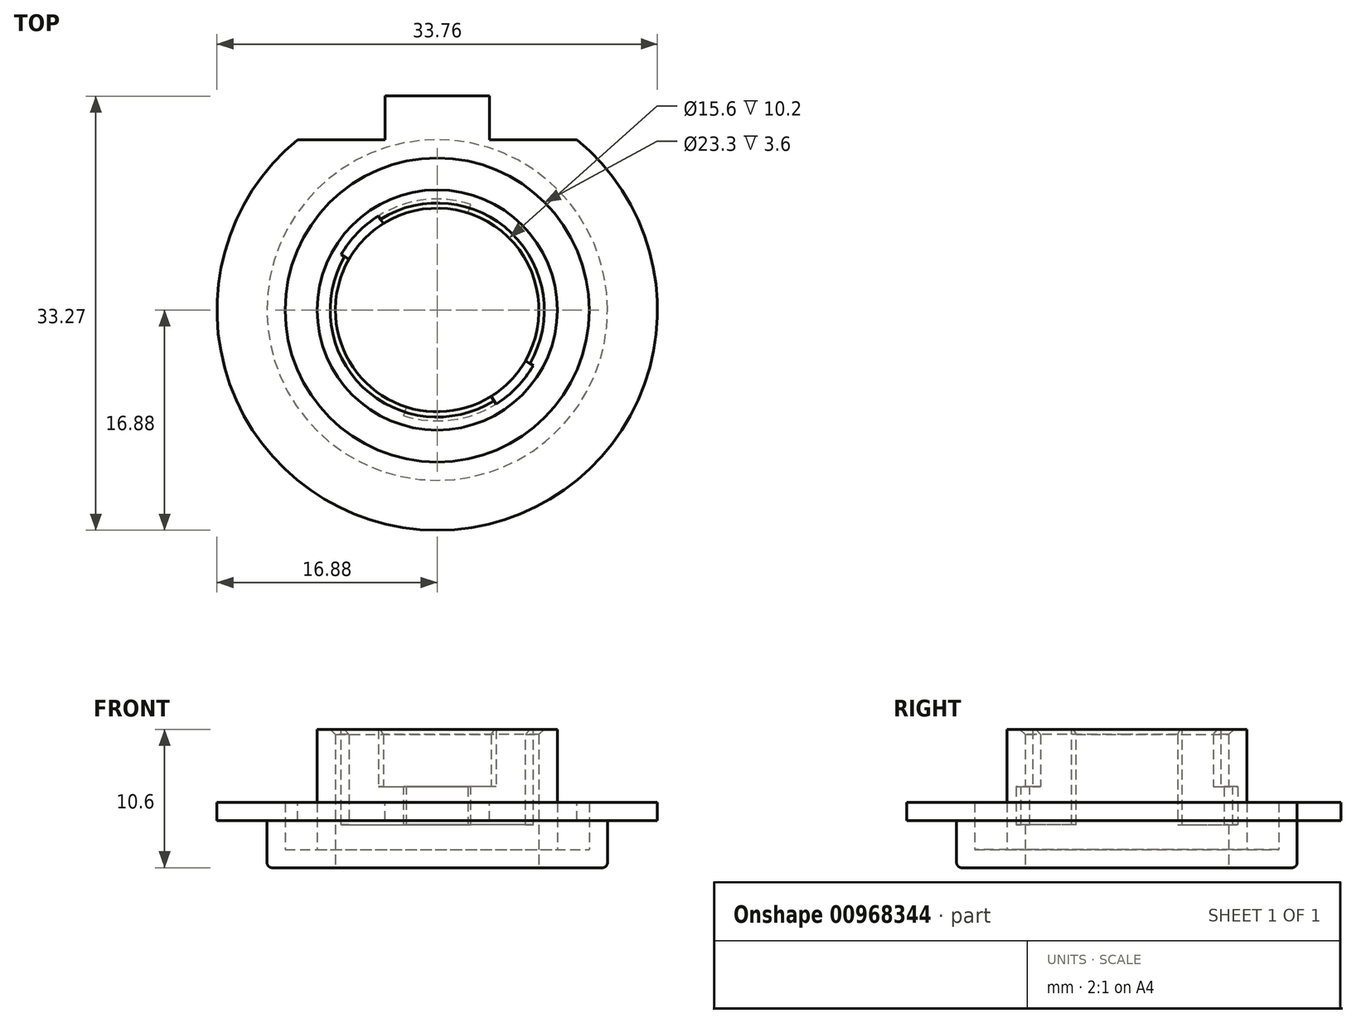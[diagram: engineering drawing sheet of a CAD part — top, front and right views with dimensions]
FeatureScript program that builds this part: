
annotation { "Feature Type Name" : "Feature", "Feature Type Description" : "" }
export const myFeature = defineFeature(function(context is Context, id is Id, definition is map)
    precondition{}
    {
        {
            var Q0;
            Q0=qCreatedBy(makeId("Front.planeOp"),FACE);
            var sketch = newSketch(context, id + "F0", { "sketchPlane" : qUnion([Q0])});
            skLineSegment(sketch, "E0", {"start": v(0, 0) * mm, "end": v(0, 105.8) * mm, "construction": true});
            skLineSegment(sketch, "E1", {"start": v(-7.8, 15.02) * mm, "end": v(-13.05, 15.02) * mm});
            skLineSegment(sketch, "E2", {"start": v(-13.05, 15.02) * mm, "end": v(-13.05, 18.62) * mm});
            skLineSegment(sketch, "E3", {"start": v(-13.05, 18.62) * mm, "end": v(-16.88, 18.62) * mm});
            skLineSegment(sketch, "E4", {"start": v(-7.8, 25.62) * mm, "end": v(-7.8, 15.02) * mm});
            skLineSegment(sketch, "E5.0", {"start": v(-11.65, 20.02) * mm, "end": v(-16.88, 20.02) * mm});
            skLineSegment(sketch, "E5.1", {"start": v(-11.65, 16.42) * mm, "end": v(-11.65, 20.02) * mm});
            skLineSegment(sketch, "E5.2", {"start": v(-9.2, 16.42) * mm, "end": v(-11.65, 16.42) * mm});
            skLineSegment(sketch, "E5.3", {"start": v(-9.2, 25.62) * mm, "end": v(-9.2, 16.42) * mm});
            skLineSegment(sketch, "E6", {"start": v(-9.2, 25.62) * mm, "end": v(-7.8, 25.62) * mm});
            skLineSegment(sketch, "E7", {"start": v(-16.88, 20.02) * mm, "end": v(-16.88, 18.62) * mm});
            skSolve(sketch);
        }
        {
            var Q0;
            Q0=makeQuery(id+"F0.imprint","IMPRINT",FACE,{"disambiguationData":[TD([[makeQuery(id+"F0.imprint","IMPRINT",EDGE,{"derivedFrom":sQuery(id+"F0.wireOp",EDGE,"E1")}),-1.0]])]});
            var Q1;
            Q1=sQuery(id+"F0.wireOp",EDGE,"E0");
            revolve(context, id + "F1", {"entities" : qUnion([Q0]), "axis" : qUnion([Q1]), "revolveType" : RevolveType.FULL});
        }
        {
            var Q0;
            Q0=makeQuery(id+"F1.opRevolve","SWEPT_FACE",FACE,{"disambiguationData":[OSD([sQuery(id+"F0.wireOp",EDGE,"E5.0")])]});
            var sketch = newSketch(context, id + "F2", { "sketchPlane" : qUnion([Q0])});
            skLineSegment(sketch, "E8", {"start": v(0, 19.6) * mm, "end": v(0, -24.8) * mm, "construction": true});
            skLineSegment(sketch, "E9", {"start": v(-16.15, 13.05) * mm, "end": v(16.92, 13.05) * mm, "construction": true});
            skLineSegment(sketch, "E10", {"start": v(-4, 16.4) * mm, "end": v(-4, 13.05) * mm});
            skLineSegment(sketch, "E11", {"start": v(-4, 13.05) * mm, "end": v(-10.7, 13.05) * mm});
            skLineSegment(sketch, "E12", {"start": v(-4, 16.4) * mm, "end": v(4, 16.4) * mm});
            skLineSegment(sketch, "E13", {"start": v(4, 16.4) * mm, "end": v(4, 13.05) * mm});
            skLineSegment(sketch, "E14", {"start": v(4, 13.05) * mm, "end": v(10.7, 13.05) * mm});
            skCircle(sketch, "E15.0", {"center": v(0, 0) * mm, "radius": 13.05 * mm});
            skSolve(sketch);
        }
        {
            var Q0;
            {var subQ0=sQuery(id+"F2.wireOp",EDGE,"E10");Q0=makeQuery(id+"F2.imprint","IMPRINT",FACE,{"disambiguationData":[TD([[makeQuery(id+"F2.imprint","IMPRINT",EDGE,{"derivedFrom":subQ0}),-1.0]])]});}
            var Q1;
            {var subQ0=sQuery(id+"F2.wireOp",EDGE,"E13");Q1=makeQuery(id+"F2.imprint","IMPRINT",FACE,{"disambiguationData":[TD([[makeQuery(id+"F2.imprint","IMPRINT",EDGE,{"derivedFrom":subQ0}),1.0]])]});}
            var Q2;
            {var subQ0=sQuery(id+"F2.wireOp",EDGE,"E12");Q2=makeQuery(id+"F2.imprint","IMPRINT",FACE,{"disambiguationData":[TD([[makeQuery(id+"F2.imprint","IMPRINT",EDGE,{"derivedFrom":subQ0}),1.0]])]});}
            extrude(context, id + "F3", {"entities" : qUnion([Q0, Q1, Q2]), "operationType" : NewBodyOperationType.REMOVE, "endBound" : BoundingType.THROUGH_ALL, "oppositeDirection" : true, "depth" : 25 * mm, "offsetDistance" : 25 * mm});
        }
        {
            var Q0;
            Q0=qCreatedBy(makeId("Right.planeOp"),FACE);
            var sketch = newSketch(context, id + "F4", { "sketchPlane" : qUnion([Q0])});
            skLineSegment(sketch, "E16", {"start": v(7.8, 18.32) * mm, "end": v(8.5, 18.32) * mm});
            skLineSegment(sketch, "E17", {"start": v(8.5, 18.32) * mm, "end": v(8.5, 21.22) * mm});
            skLineSegment(sketch, "E18", {"start": v(8.5, 21.22) * mm, "end": v(7.8, 21.22) * mm});
            skLineSegment(sketch, "E19", {"start": v(7.8, 25.62) * mm, "end": v(7.8, 15.02) * mm});
            skLineSegment(sketch, "E20", {"start": v(-7.8, 15.02) * mm, "end": v(-7.8, 25.62) * mm});
            skLineSegment(sketch, "E21", {"start": v(9.2, 25.62) * mm, "end": v(9.2, 16.42) * mm});
            skLineSegment(sketch, "E22", {"start": v(-9.2, 16.42) * mm, "end": v(-9.2, 25.62) * mm});
            skLineSegment(sketch, "E23.MirrorCS", {"start": v(-7.8, 18.32) * mm, "end": v(-8.5, 18.32) * mm});
            skLineSegment(sketch, "E24.MirrorCS", {"start": v(-8.5, 18.32) * mm, "end": v(-8.5, 21.22) * mm});
            skLineSegment(sketch, "E25.MirrorCS", {"start": v(-8.5, 21.22) * mm, "end": v(-7.8, 21.22) * mm});
            skSolve(sketch);
        }
        {
            var Q0;
            Q0=qSketchRegion(id+"F4",true);
            var Q1;
            Q1=makeQuery(id+"F1.opRevolve","SWEPT_EDGE",EDGE,{"disambiguationData":[OSD([sQuery(id+"F0.wireOp",EDGE,"E4"),sQuery(id+"F0.wireOp",EDGE,"E6")])]});
            revolve(context, id + "F5", {"operationType" : NewBodyOperationType.REMOVE, "entities" : qUnion([Q0]), "axis" : qUnion([Q1]), "revolveType" : RevolveType.TWO_DIRECTIONS, "oppositeDirection" : true, "angle" : 60 * degree, "angleBack" : 342.41 * degree});
        }
        {
            var Q0;
            Q0=qCreatedBy(makeId("Right.planeOp"),FACE);
            var sketch = newSketch(context, id + "F6", { "sketchPlane" : qUnion([Q0])});
            skLineSegment(sketch, "E26", {"start": v(-7.8, 21.22) * mm, "end": v(-7.8, 25.62) * mm, "construction": true});
            skLineSegment(sketch, "E27", {"start": v(7.8, 25.62) * mm, "end": v(7.8, 21.22) * mm, "construction": true});
            skLineSegment(sketch, "E28", {"start": v(7.8, 18.32) * mm, "end": v(7.8, 15.02) * mm, "construction": true});
            skLineSegment(sketch, "E29", {"start": v(-7.8, 15.02) * mm, "end": v(-7.8, 18.32) * mm, "construction": true});
            skLineSegment(sketch, "E30.0", {"start": v(13.05, 15.02) * mm, "end": v(-13.05, 15.02) * mm, "construction": true});
            skLineSegment(sketch, "E31", {"start": v(8.5, 18.32) * mm, "end": v(8.5, 21.22) * mm, "construction": true});
            skLineSegment(sketch, "E32", {"start": v(7.8, 18.32) * mm, "end": v(8.5, 18.32) * mm, "construction": true});
            skLineSegment(sketch, "E33", {"start": v(8.5, 21.22) * mm, "end": v(7.8, 21.22) * mm, "construction": true});
            skLineSegment(sketch, "E34", {"start": v(7.8, 18.32) * mm, "end": v(8.5, 18.32) * mm});
            skLineSegment(sketch, "E35", {"start": v(8.5, 25.62) * mm, "end": v(7.8, 25.62) * mm});
            skLineSegment(sketch, "E36", {"start": v(8.5, 25.62) * mm, "end": v(8.5, 18.32) * mm});
            skLineSegment(sketch, "E37", {"start": v(7.8, 25.62) * mm, "end": v(7.8, 18.32) * mm});
            skLineSegment(sketch, "E38.MirrorCS", {"start": v(-7.8, 18.32) * mm, "end": v(-8.5, 18.32) * mm, "construction": true});
            skLineSegment(sketch, "E39.MirrorCS", {"start": v(-7.8, 18.32) * mm, "end": v(-8.5, 18.32) * mm});
            skLineSegment(sketch, "E40.MirrorCS", {"start": v(-8.5, 25.62) * mm, "end": v(-7.8, 25.62) * mm});
            skLineSegment(sketch, "E41.MirrorCS", {"start": v(-7.8, 25.62) * mm, "end": v(-7.8, 21.22) * mm, "construction": true});
            skLineSegment(sketch, "E42.MirrorCS", {"start": v(-8.5, 18.32) * mm, "end": v(-8.5, 21.22) * mm, "construction": true});
            skLineSegment(sketch, "E43.MirrorCS", {"start": v(-8.5, 25.62) * mm, "end": v(-8.5, 18.32) * mm});
            skLineSegment(sketch, "E44.MirrorCS", {"start": v(-7.8, 25.62) * mm, "end": v(-7.8, 18.32) * mm});
            skSolve(sketch);
        }
        {
            var Q0;
            Q0=qSketchRegion(id+"F6",true);
            var Q1;
            Q1=makeQuery(id+"F1.opRevolve","SWEPT_FACE",FACE,{"disambiguationData":[OSD([sQuery(id+"F0.wireOp",EDGE,"E4")])]});
            revolve(context, id + "F7", {"operationType" : NewBodyOperationType.REMOVE, "entities" : qUnion([Q0]), "axis" : qUnion([Q1]), "revolveType" : RevolveType.TWO_DIRECTIONS, "oppositeDirection" : true, "angle" : 328 * degree, "angleBack" : 300 * degree});
        }
        {
            var Q0;
            {var subQ0=sQuery(id+"F0.wireOp",EDGE,"E4");var subQ1=sQuery(id+"F0.wireOp",EDGE,"E6");Q0=makeQuery(id+"F7.boolean.opBoolean","SPLIT",EDGE,{"disambiguationData":[TD([makeQuery(id+"F5.boolean.opBoolean","COPY",FACE,{"derivedFrom":makeQuery(id+"F5.opRevolve","CAP_FACE",FACE,{"disambiguationData":[OSD([sQuery(id+"F4.wireOp",EDGE,"E20"),sQuery(id+"F4.wireOp",EDGE,"E23.MirrorCS"),sQuery(id+"F4.wireOp",EDGE,"E24.MirrorCS"),sQuery(id+"F4.wireOp",EDGE,"E25.MirrorCS")])],"isStart":false})})])],"derivedFrom":makeQuery(id+"F1.opRevolve","SWEPT_EDGE",EDGE,{"disambiguationData":[OSD([subQ0,subQ1])]})});}
            var Q1;
            {var subQ0=sQuery(id+"F0.wireOp",EDGE,"E6");var subQ1=sQuery(id+"F0.wireOp",EDGE,"E4");Q1=makeQuery(id+"F7.boolean.opBoolean","SPLIT",EDGE,{"disambiguationData":[TD([makeQuery(id+"F5.boolean.opBoolean","COPY",FACE,{"derivedFrom":makeQuery(id+"F5.opRevolve","CAP_FACE",FACE,{"disambiguationData":[OSD([sQuery(id+"F4.wireOp",EDGE,"E16"),sQuery(id+"F4.wireOp",EDGE,"E17"),sQuery(id+"F4.wireOp",EDGE,"E18"),sQuery(id+"F4.wireOp",EDGE,"E19")]),OD(0.0)],"isStart":false})})])],"derivedFrom":makeQuery(id+"F1.opRevolve","SWEPT_EDGE",EDGE,{"disambiguationData":[OSD([subQ1,subQ0])]})});}
            chamfer(context, id + "F8", {"entities" : qUnion([Q0, Q1]), "width" : 0.4 * mm, "tangentPropagation" : true});
        }
        {
            var Q0;
            Q0=makeQuery(id+"F1.opRevolve","SWEPT_EDGE",EDGE,{"disambiguationData":[OSD([sQuery(id+"F0.wireOp",EDGE,"E1"),sQuery(id+"F0.wireOp",EDGE,"E2")])]});
            fillet(context, id + "F9", {"entities" : qUnion([Q0]), "radius" : 0.4 * mm, "tangentPropagation" : true, "allowEdgeOverflow" : false});
        }
    });
